# Revit family: Prises non verrouilllées 200_250 V
name_source: partatom
category: Installations électriques
revit_build: Autodesk Revit 2018 (Build: 20170223_1515(x64)
units: mm (PartAtom-declared; Revit-internal decimal feet)

## family parameters
Conserver l'orientation des annotations = Non
Cote de connecteur circulaire = Utiliser le diamètre
Couper avec des vides une fois chargée = Non
Hôte = Face
Partagée = Non
Point de calcul de pièce = Non
Type d'élément = Normal

## types (19) — shared parameters
Couleur caractéristique = bleu
Elévation par défaut = 1000 mm  [stored 3.28084 ft]
Fabricant = Legrand
Famille produit = 0854-P17 TEMPRA PRO
Prise au standard international pour montage encastré ou saillie avec accessoire permet la connexion d'appareils de puissance = Prise au standard international pour montage encastré ou saillie avec accessoire permet la connexion d'appareils de puissance
Standard CEI ou NFC = CEI
Température maximum d'utilisation = 40
Température minimum d'utilisation = -25
Tension V = 230 V  50/60 Hz  bleu
matériau du boitier = plastique
résistance aux chocs IK = 9
type de raccordement = bornes à vis

## per-type parameters (varying)
| type | Description | Intensité A | Nombre de pôles | Position de la Terre h | Température minimum d'installation | classe de protection IP | entraxe de fixation horizontal mm | entraxe de fixation vertical mm | hauteur mm | installation Encastrée E ou Saillie S | largeur mm | profondeur d'encastrement mm | profondeur mm | sans halogène |
| P17 Pro - IP66/67 - 63 A - 3P+N+T | LG-555586_Panneau de montage prise P17 Pro - IP66/67 - 200/250 V - 63 A - 3P+N+T | 63 A | 5 | 9 | -5 |  | 77 mm | 85 mm | 106 mm  [stored 0.347769 ft] | encastré | 106 mm  [stored 0.347769 ft] | 84 mm  [stored 0.275591 ft] | 161 mm | Non |
| P17 Pro - IP66/67 - 63 A - 3P+T | LG-555585_Panneau de montage prise P17 Pro - IP66/67 - 200/250 V - 63 A - 3P+T | 63 A | 4 | 9 | -5 |  | 77 mm | 85 mm | 106 mm  [stored 0.347769 ft] | encastré | 106 mm  [stored 0.347769 ft] | 84 mm  [stored 0.275591 ft] | 161 mm | Non |
| P17 Pro - IP66/67 - 63 A - 2P+T | LG-555584_Panneau de montage prise P17 Pro - IP66/67 - 200/250 V - 63 A - 2P+T | 63 A | 3 | 6 | -5 |  | 77 mm | 85 mm | 106 mm  [stored 0.347769 ft] | encastré | 106 mm  [stored 0.347769 ft] | 84 mm  [stored 0.275591 ft] | 161 mm | Non |
| P17 - IP66/67 - 32 A - 3P+N+T | LG-555486_Panneau de montage prise P17 - IP66/67 - 200/250 V - 32 A - 3P+N+T | 32 A | 5 | 9 | -5 |  | 70 mm | 70 mm | 84 mm  [stored 0.275591 ft] | encastré et saillie | 84 mm  [stored 0.275591 ft] | 43 mm  [stored 0.141076 ft] | 94 mm  [stored 0.308399 ft] | Non |
| P17 - IP66/67 - 32 A - 3P+T | LG-555485_Panneau de montage prise P17 - IP66/67 - 200/250 V - 32 A - 3P+T | 32 A | 4 | 9 | -5 |  | 70 mm | 70 mm | 84 mm  [stored 0.275591 ft] | encastré et saillie | 84 mm  [stored 0.275591 ft] | 42 mm | 92 mm | Non |
| P17 - IP66/67 - 32 A - 2P+T | LG-555484_Panneau de montage prise P17 - IP66/67 - 200/250 V - 32 A - 2P+T | 32 A | 3 | 6 | -5 |  | 70 mm | 70 mm | 84 mm  [stored 0.275591 ft] | encastré et saillie | 84 mm  [stored 0.275591 ft] | 42 mm | 92 mm | Non |
| P17 - IP66/67 - 16 A - 3P+N+T | LG-555386_Panneau de montage prise P17 - IP66/67 - 200/250 V - 16 A - 3P+N+T | 16 A | 5 | 9 | -5 |  | 70 mm | 70 mm | 84 mm  [stored 0.275591 ft] | encastré et saillie | 84 mm  [stored 0.275591 ft] | 37 mm  [stored 0.121391 ft] | 81 mm | Non |
| P17 - IP66/67 - 16 A - 3P+T | LG-555385_Panneau de montage prise P17 - IP66/67 - 200/250 V - 16 A - 3P+T | 16 A | 4 | 9 | -5 |  | 70 mm | 70 mm | 84 mm  [stored 0.275591 ft] | encastré et saillie | 84 mm  [stored 0.275591 ft] | 36 mm | 79 mm | Non |
| P17 - IP66/67 - 16 A - 2P+T | LG-555384_Panneau de montage prise P17 - IP66/67 - 200/250 V - 16 A - 2P+T | 16 A | 3 | 6 | -5 |  | 70 mm | 70 mm | 84 mm  [stored 0.275591 ft] | encastré et saillie | 84 mm  [stored 0.275591 ft] | 34 mm | 76 mm | Non |
| P17 - IP44 - 32 A - 3P+N+T | LG-555286_Panneau de montage prise P17 - sortie inclinée - IP44 - 200/250 V - 32 A - 3P+N+T | 32 A | 5 | 9 | -5 | IP44 | 70 mm | 70 mm | 84 mm  [stored 0.275591 ft] | encastré et saillie | 84 mm  [stored 0.275591 ft] | 43 mm  [stored 0.141076 ft] | 89 mm  [stored 0.291995 ft] | Oui |
| P17 - IP44 - 32 A - 3P+T | LG-555285_Panneau de montage prise P17 - sortie inclinée - IP44 - 200/250 V - 32 A - 3P+T | 32 A | 4 | 9 | -5 | IP44 | 70 mm | 70 mm | 84 mm  [stored 0.275591 ft] | encastré et saillie | 84 mm  [stored 0.275591 ft] | 42 mm | 87 mm | Oui |
| P17 - IP44 - 32 A - 2P+T | LG-555284_Panneau de montage prise P17 - sortie inclinée - IP44 - 200/250 V - 32 A - 2P+T | 32 A | 3 | 6 | -5 | IP44 | 70 mm | 70 mm | 84 mm  [stored 0.275591 ft] | encastré et saillie | 84 mm  [stored 0.275591 ft] | 42 mm | 87 mm | Oui |
| P17 - IP44 - 16A - 3P+N+T | LG-555186_Panneau de montage prise P17 - sortie inclinée - IP44 - 200/250 V - 16 A - 3P+N+T | 16 A | 5 | 9 | -5 | IP44 | 70 mm | 70 mm | 84 mm  [stored 0.275591 ft] | encastré et saillie | 84 mm  [stored 0.275591 ft] | 37 mm  [stored 0.121391 ft] | 76 mm | Oui |
| P17 - IP44 - 16A - 3P+T | LG-555185_Panneau de montage prise P17 - sortie inclinée - IP44 - 200/250 V - 16 A - 3P+T | 16 A | 4 | 9 | -5 | IP44 | 70 mm | 70 mm | 84 mm  [stored 0.275591 ft] | encastré et saillie | 84 mm  [stored 0.275591 ft] | 36 mm | 74 mm | Oui |
| P17 - IP44 - 16A - 2P+T 1 | LG-555184_Panneau de montage prise P17 - sortie inclinée - IP44 - 200/250 V - 16 A - 2P+T | 16 A | 3 | 6 | -5 | IP44 | 70 mm | 70 mm | 84 mm  [stored 0.275591 ft] | encastré et saillie | 84 mm  [stored 0.275591 ft] | 34 mm | 71 mm | Oui |
| P17 - 32A - 2P+T - IP44 | LG-090169_Panneau de montage prise P17 32A 2P+T 200/250V IP44 | 32 A | 3 | 6 | -5 | IP44 | 70 mm | 70 mm | 84 mm  [stored 0.275591 ft] | encastré et saillie | 84 mm  [stored 0.275591 ft] | 42 mm | 87 mm | Oui |
| P17 - 16A - 2P+T - IP44 | LG-090168_Panneau de montage prise P17 16A 2P+T 200/250V IP44 | 16 A | 3 | 6 | -5 | IP44 | 70 mm | 70 mm | 84 mm  [stored 0.275591 ft] | encastré et saillie | 84 mm  [stored 0.275591 ft] | 34 mm | 71 mm | Oui |
| P17 - IP44 - 32A - 3P+T | LG-058054_Panneau de montage prise P17- IP44 - sortie droite - 200/250 V - 32 A - 2P+T | 32 A | 3 | 6 |  | IP44 | 60 mm  [stored 0.19685 ft] | 60 mm  [stored 0.19685 ft] | 98 mm | encastré | 75 mm | 31 mm | 93 mm | Oui |
| P17 - IP44 - 16A - 2P+T | LG-057354_Panneau de montage prise P17 - IP44 - sortie droite - 200/250 V - 16 A - 2P+T | 16 A | 3 | 6 |  | IP44 | 47 mm | 47 mm | 58 mm  [stored 0.190289 ft] | encastré | 58 mm  [stored 0.190289 ft] | 22 mm  [stored 0.0721785 ft] | 72 mm | Oui |

note: [stored X ft] marks values corroborated as IEEE doubles in the binary element streams (Revit-internal decimal feet)
